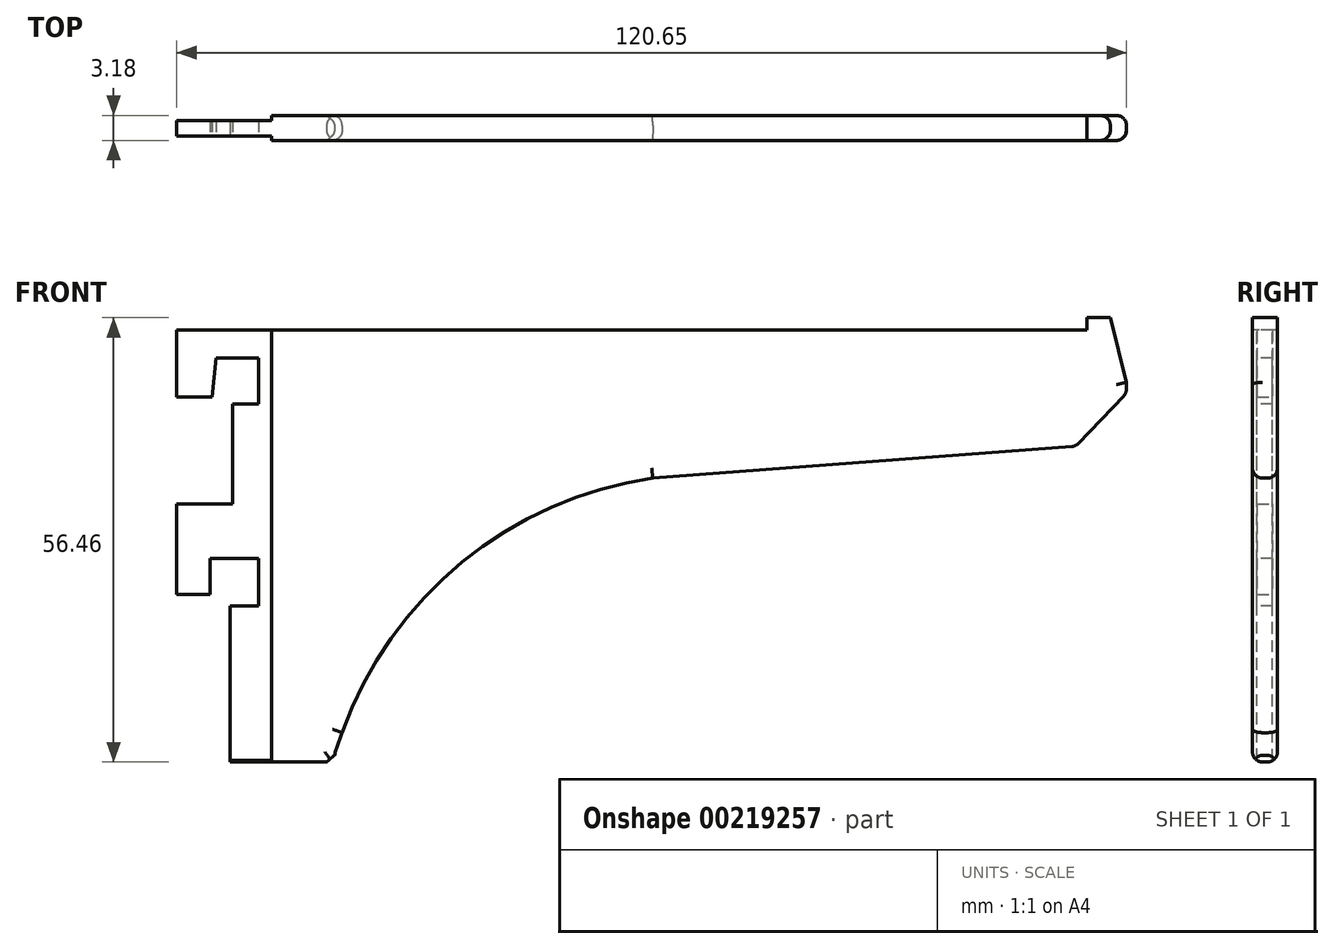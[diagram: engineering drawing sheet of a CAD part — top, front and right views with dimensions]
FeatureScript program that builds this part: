
annotation { "Feature Type Name" : "Feature", "Feature Type Description" : "" }
export const myFeature = defineFeature(function(context is Context, id is Id, definition is map)
    precondition{}
    {
        {
            var Q0;
            Q0=qCreatedBy(makeId("Front.planeOp"),FACE);
            var sketch = newSketch(context, id + "F0", { "sketchPlane" : qUnion([Q0])});
            skLineSegment(sketch, "E0.bottom", {"start": v(-45.03, 28.7) * mm, "end": v(75.62, 28.7) * mm});
            skLineSegment(sketch, "E0.top", {"start": v(-45.03, -28.46) * mm, "end": v(75.62, -28.46) * mm});
            skLineSegment(sketch, "E0.left", {"start": v(-45.03, 28.7) * mm, "end": v(-45.03, -28.46) * mm});
            skLineSegment(sketch, "E0.right", {"start": v(75.62, 28.7) * mm, "end": v(75.62, -28.46) * mm});
            skSolve(sketch);
        }
        {
            var Q0;
            Q0=qCreatedBy(makeId("Front.planeOp"),FACE);
            var sketch = newSketch(context, id + "F1", { "sketchPlane" : qUnion([Q0])});
            skLineSegment(sketch, "E1.bottom", {"start": v(70.6, 30.4) * mm, "end": v(-50.82, 30.4) * mm});
            skLineSegment(sketch, "E1.top", {"start": v(70.6, 27.11) * mm, "end": v(-50.82, 27.11) * mm});
            skLineSegment(sketch, "E1.left", {"start": v(70.6, 30.4) * mm, "end": v(70.6, 27.11) * mm});
            skLineSegment(sketch, "E1.right", {"start": v(-50.82, 30.4) * mm, "end": v(-50.82, 27.11) * mm});
            skSolve(sketch);
        }
        {
            var Q0;
            Q0=makeQuery(id+"F0.imprint","IMPRINT",FACE,{"disambiguationData":[TD([[makeQuery(id+"F0.imprint","IMPRINT",EDGE,{"derivedFrom":sQuery(id+"F0.wireOp",EDGE,"E0.bottom")}),-1.0]])]});
            extrude(context, id + "F2", {"entities" : qUnion([Q0]), "depth" : 3.17 * mm});
        }
        {
            var Q0;
            Q0=makeQuery(id+"F1.imprint","IMPRINT",FACE,{"disambiguationData":[TD([[makeQuery(id+"F1.imprint","IMPRINT",EDGE,{"derivedFrom":sQuery(id+"F1.wireOp",EDGE,"E1.bottom")}),1.0]])]});
            extrude(context, id + "F3", {"entities" : qUnion([Q0]), "operationType" : NewBodyOperationType.REMOVE, "endBound" : BoundingType.SYMMETRIC, "oppositeDirection" : true, "depth" : 98.55 * mm});
        }
        {
            var Q0;
            Q0=qCreatedBy(makeId("Front.planeOp"),FACE);
            var sketch = newSketch(context, id + "F4", { "sketchPlane" : qUnion([Q0])});
            skLineSegment(sketch, "E2.bottom", {"start": v(-47.7, 18.6) * mm, "end": v(-40.56, 18.6) * mm});
            skLineSegment(sketch, "E2.top", {"start": v(-47.7, 5.01) * mm, "end": v(-37.94, 5.01) * mm});
            skLineSegment(sketch, "E2.left", {"start": v(-47.7, 18.6) * mm, "end": v(-47.7, 5.01) * mm});
            skLineSegment(sketch, "E2.right", {"start": v(-37.94, 17.73) * mm, "end": v(-37.94, 5.01) * mm});
            skLineSegment(sketch, "E3.bottom", {"start": v(-47.25, -6.5) * mm, "end": v(-40.79, -6.5) * mm});
            skLineSegment(sketch, "E3.top", {"start": v(-47.25, -35.88) * mm, "end": v(-38.26, -35.88) * mm});
            skLineSegment(sketch, "E3.left", {"start": v(-47.25, -6.5) * mm, "end": v(-47.25, -35.88) * mm});
            skLineSegment(sketch, "E3.right", {"start": v(-38.26, -7.92) * mm, "end": v(-38.26, -27.77) * mm});
            skLineSegment(sketch, "E4.bottom", {"start": v(-40.02, 23.54) * mm, "end": v(-34.65, 23.54) * mm});
            skLineSegment(sketch, "E4.top", {"start": v(-37.94, 17.73) * mm, "end": v(-34.65, 17.73) * mm});
            skLineSegment(sketch, "E4.right", {"start": v(-34.65, 23.54) * mm, "end": v(-34.65, 17.73) * mm});
            skLineSegment(sketch, "E5.bottom", {"start": v(-34.65, -1.9) * mm, "end": v(-40.79, -1.9) * mm});
            skLineSegment(sketch, "E5.top", {"start": v(-34.65, -7.92) * mm, "end": v(-38.26, -7.92) * mm});
            skLineSegment(sketch, "E5.left", {"start": v(-34.65, -1.9) * mm, "end": v(-34.65, -7.92) * mm});
            skLineSegment(sketch, "E5.right", {"start": v(-40.79, -1.9) * mm, "end": v(-40.79, -6.5) * mm});
            skLineSegment(sketch, "E6", {"start": v(75.85, 19.37) * mm, "end": v(69.17, 12.36) * mm});
            skLineSegment(sketch, "E7", {"start": v(69.17, 12.36) * mm, "end": v(15.45, 8.3) * mm});
            skLineSegment(sketch, "E8", {"start": v(-25, -26.9) * mm, "end": v(-25.99, -27.77) * mm});
            skLineSegment(sketch, "E9", {"start": v(-25.99, -27.77) * mm, "end": v(-38.26, -27.77) * mm});
            skLineSegment(sketch, "E10", {"start": v(-38.26, -35.88) * mm, "end": v(78.92, -35.88) * mm});
            skLineSegment(sketch, "E11", {"start": v(78.92, -35.88) * mm, "end": v(78.92, 19.04) * mm});
            skArc(sketch, "E12", {"start": v(15.45, 8.3) * mm, "mid": v(-8.78, -2.37) * mm, "end": v(-24.01, -24.04) * mm});
            skArc(sketch, "E13", {"start": v(-24.01, -24.04) * mm, "mid": v(-24.52, -25.47) * mm, "end": v(-25, -26.9) * mm});
            skLineSegment(sketch, "E14", {"start": v(-40.02, 23.54) * mm, "end": v(-40.56, 18.6) * mm});
            skLineSegment(sketch, "E15", {"start": v(75.85, 19.37) * mm, "end": v(72.97, 31.12) * mm});
            skLineSegment(sketch, "E16", {"start": v(72.97, 31.12) * mm, "end": v(78.9, 31.12) * mm});
            skLineSegment(sketch, "E17", {"start": v(78.9, 31.12) * mm, "end": v(78.92, 19.04) * mm});
            skSolve(sketch);
        }
        {
            var Q0;
            Q0 = qSketchRegion(id + "F4", true);
            extrude(context, id + "F5", {"entities" : qUnion([Q0]), "operationType" : NewBodyOperationType.REMOVE, "endBound" : BoundingType.SYMMETRIC, "oppositeDirection" : true, "depth" : 25.4 * mm});
        }
        {
            var Q0;
            Q0=makeQuery(id+"F5.boolean.opBoolean","INTERSECT",EDGE,{"derivedFrom":[makeQuery(id+"F2.opExtrude","CAP_FACE",FACE,{"disambiguationData":[OSD([sQuery(id+"F0.wireOp",EDGE,"E0.bottom"),sQuery(id+"F0.wireOp",EDGE,"E0.top"),sQuery(id+"F0.wireOp",EDGE,"E0.left"),sQuery(id+"F0.wireOp",EDGE,"E0.right")])],"isStart":false}),makeQuery(id+"F5.opExtrude","SWEPT_FACE",FACE,{"disambiguationData":[OSD([sQuery(id+"F4.wireOp",EDGE,"E12")])]})]});
            var Q1;
            Q1=makeQuery(id+"F5.boolean.opBoolean","INTERSECT",EDGE,{"derivedFrom":[makeQuery(id+"F2.opExtrude","CAP_FACE",FACE,{"disambiguationData":[OSD([sQuery(id+"F0.wireOp",EDGE,"E0.bottom"),sQuery(id+"F0.wireOp",EDGE,"E0.top"),sQuery(id+"F0.wireOp",EDGE,"E0.left"),sQuery(id+"F0.wireOp",EDGE,"E0.right")])],"isStart":false}),makeQuery(id+"F5.opExtrude","SWEPT_FACE",FACE,{"disambiguationData":[OSD([sQuery(id+"F4.wireOp",EDGE,"E7")])]})]});
            var Q2;
            Q2=makeQuery(id+"F5.boolean.opBoolean","INTERSECT",EDGE,{"derivedFrom":[makeQuery(id+"F2.opExtrude","CAP_FACE",FACE,{"disambiguationData":[OSD([sQuery(id+"F0.wireOp",EDGE,"E0.bottom"),sQuery(id+"F0.wireOp",EDGE,"E0.top"),sQuery(id+"F0.wireOp",EDGE,"E0.left"),sQuery(id+"F0.wireOp",EDGE,"E0.right")])],"isStart":false}),makeQuery(id+"F5.opExtrude","SWEPT_FACE",FACE,{"disambiguationData":[OSD([sQuery(id+"F4.wireOp",EDGE,"E6")])]})]});
            var Q3;
            Q3=makeQuery(id+"F5.boolean.opBoolean","INTERSECT",EDGE,{"derivedFrom":[makeQuery(id+"F2.opExtrude","CAP_FACE",FACE,{"disambiguationData":[OSD([sQuery(id+"F0.wireOp",EDGE,"E0.bottom"),sQuery(id+"F0.wireOp",EDGE,"E0.top"),sQuery(id+"F0.wireOp",EDGE,"E0.left"),sQuery(id+"F0.wireOp",EDGE,"E0.right")])],"isStart":true}),makeQuery(id+"F5.opExtrude","SWEPT_FACE",FACE,{"disambiguationData":[OSD([sQuery(id+"F4.wireOp",EDGE,"E7")])]})]});
            var Q4;
            Q4=makeQuery(id+"F5.boolean.opBoolean","INTERSECT",EDGE,{"derivedFrom":[makeQuery(id+"F2.opExtrude","CAP_FACE",FACE,{"disambiguationData":[OSD([sQuery(id+"F0.wireOp",EDGE,"E0.bottom"),sQuery(id+"F0.wireOp",EDGE,"E0.top"),sQuery(id+"F0.wireOp",EDGE,"E0.left"),sQuery(id+"F0.wireOp",EDGE,"E0.right")])],"isStart":true}),makeQuery(id+"F5.opExtrude","SWEPT_FACE",FACE,{"disambiguationData":[OSD([sQuery(id+"F4.wireOp",EDGE,"E6")])]})]});
            var Q5;
            Q5=makeQuery(id+"F5.boolean.opBoolean","INTERSECT",EDGE,{"derivedFrom":[makeQuery(id+"F2.opExtrude","CAP_FACE",FACE,{"disambiguationData":[OSD([sQuery(id+"F0.wireOp",EDGE,"E0.bottom"),sQuery(id+"F0.wireOp",EDGE,"E0.top"),sQuery(id+"F0.wireOp",EDGE,"E0.left"),sQuery(id+"F0.wireOp",EDGE,"E0.right")])],"isStart":true}),makeQuery(id+"F5.opExtrude","SWEPT_FACE",FACE,{"disambiguationData":[OSD([sQuery(id+"F4.wireOp",EDGE,"E12")])]})]});
            var Q6;
            Q6=makeQuery(id+"F5.boolean.opBoolean","INTERSECT",EDGE,{"derivedFrom":[makeQuery(id+"F2.opExtrude","CAP_FACE",FACE,{"disambiguationData":[OSD([sQuery(id+"F0.wireOp",EDGE,"E0.bottom"),sQuery(id+"F0.wireOp",EDGE,"E0.top"),sQuery(id+"F0.wireOp",EDGE,"E0.left"),sQuery(id+"F0.wireOp",EDGE,"E0.right")])],"isStart":false}),makeQuery(id+"F5.opExtrude","SWEPT_FACE",FACE,{"disambiguationData":[OSD([sQuery(id+"F4.wireOp",EDGE,"E9")])]})]});
            var Q7;
            Q7=makeQuery(id+"F5.boolean.opBoolean","INTERSECT",EDGE,{"derivedFrom":[makeQuery(id+"F2.opExtrude","CAP_FACE",FACE,{"disambiguationData":[OSD([sQuery(id+"F0.wireOp",EDGE,"E0.bottom"),sQuery(id+"F0.wireOp",EDGE,"E0.top"),sQuery(id+"F0.wireOp",EDGE,"E0.left"),sQuery(id+"F0.wireOp",EDGE,"E0.right")])],"isStart":true}),makeQuery(id+"F5.opExtrude","SWEPT_FACE",FACE,{"disambiguationData":[OSD([sQuery(id+"F4.wireOp",EDGE,"E9")])]})]});
            var Q8;
            Q8=makeQuery(id+"F5.boolean.opBoolean","INTERSECT",EDGE,{"derivedFrom":[makeQuery(id+"F2.opExtrude","CAP_FACE",FACE,{"disambiguationData":[OSD([sQuery(id+"F0.wireOp",EDGE,"E0.bottom"),sQuery(id+"F0.wireOp",EDGE,"E0.top"),sQuery(id+"F0.wireOp",EDGE,"E0.left"),sQuery(id+"F0.wireOp",EDGE,"E0.right")])],"isStart":false}),makeQuery(id+"F5.opExtrude","SWEPT_FACE",FACE,{"disambiguationData":[OSD([sQuery(id+"F4.wireOp",EDGE,"E15")])]})]});
            var Q9;
            Q9=makeQuery(id+"F5.boolean.opBoolean","INTERSECT",EDGE,{"derivedFrom":[makeQuery(id+"F2.opExtrude","CAP_FACE",FACE,{"disambiguationData":[OSD([sQuery(id+"F0.wireOp",EDGE,"E0.bottom"),sQuery(id+"F0.wireOp",EDGE,"E0.top"),sQuery(id+"F0.wireOp",EDGE,"E0.left"),sQuery(id+"F0.wireOp",EDGE,"E0.right")])],"isStart":true}),makeQuery(id+"F5.opExtrude","SWEPT_FACE",FACE,{"disambiguationData":[OSD([sQuery(id+"F4.wireOp",EDGE,"E15")])]})]});
            var Q10;
            Q10=makeQuery(id+"F2.opExtrude","SWEPT_FACE",FACE,{"disambiguationData":[OSD([sQuery(id+"F0.wireOp",EDGE,"E0.right")])]});
            var Q11;
            Q11=makeQuery(id+"F5.boolean.opBoolean","COPY",EDGE,{"derivedFrom":makeQuery(id+"F5.opExtrude","SWEPT_EDGE",EDGE,{"disambiguationData":[OSD([sQuery(id+"F4.wireOp",EDGE,"E6"),sQuery(id+"F4.wireOp",EDGE,"E7")])]})});
            fillet(context, id + "F6", {"entities" : qUnion([Q0, Q1, Q2, Q3, Q4, Q5, Q6, Q7, Q8, Q9, Q10, Q11]), "radius" : 1.27 * mm, "tangentPropagation" : true, "allowEdgeOverflow" : false});
        }
        {
            var Q0;
            Q0=qCreatedBy(makeId("Top.planeOp"),FACE);
            var sketch = newSketch(context, id + "F7", { "sketchPlane" : qUnion([Q0])});
            skLineSegment(sketch, "E18.bottom", {"start": v(-46.85, 1.64) * mm, "end": v(-32.96, 1.64) * mm});
            skLineSegment(sketch, "E18.top", {"start": v(-46.85, -0.62) * mm, "end": v(-32.96, -0.62) * mm});
            skLineSegment(sketch, "E18.left", {"start": v(-46.85, 1.64) * mm, "end": v(-46.85, -0.62) * mm});
            skLineSegment(sketch, "E18.right", {"start": v(-32.96, 1.64) * mm, "end": v(-32.96, -0.62) * mm});
            skLineSegment(sketch, "E19.bottom", {"start": v(-46.85, -2.6) * mm, "end": v(-32.96, -2.6) * mm});
            skLineSegment(sketch, "E19.top", {"start": v(-46.85, -4.72) * mm, "end": v(-32.96, -4.72) * mm});
            skLineSegment(sketch, "E19.left", {"start": v(-46.85, -2.6) * mm, "end": v(-46.85, -4.72) * mm});
            skLineSegment(sketch, "E19.right", {"start": v(-32.96, -2.6) * mm, "end": v(-32.96, -4.72) * mm});
            skSolve(sketch);
        }
        {
            var Q0;
            Q0=makeQuery(id+"F7.imprint","IMPRINT",FACE,{"disambiguationData":[TD([[makeQuery(id+"F7.imprint","IMPRINT",EDGE,{"derivedFrom":sQuery(id+"F7.wireOp",EDGE,"E18.bottom")}),-1.0]])]});
            var Q1;
            Q1=makeQuery(id+"F7.imprint","IMPRINT",FACE,{"disambiguationData":[TD([[makeQuery(id+"F7.imprint","IMPRINT",EDGE,{"derivedFrom":sQuery(id+"F7.wireOp",EDGE,"E19.bottom")}),-1.0]])]});
            extrude(context, id + "F8", {"entities" : qUnion([Q0, Q1]), "operationType" : NewBodyOperationType.REMOVE, "endBound" : BoundingType.SYMMETRIC, "oppositeDirection" : true, "depth" : 89.56 * mm});
        }
    });
